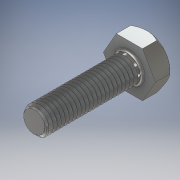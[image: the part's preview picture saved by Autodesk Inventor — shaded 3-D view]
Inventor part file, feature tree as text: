
AUTODESK INVENTOR PART (.ipt)
format: ipt  version: 2017 (Build 210142000, 142)  size: 576,512 bytes
history: native  units: mm
features: sketch x4, extrude x3, chamfer x1, fillet x1, plane x1, helix x1
ambient origin geometry x8: Origin, YZ Plane, XZ Plane, XY Plane, X Axis, Y Axis, Z Axis, Center Point
bodies: Solid1 (feature_tree)
feature tree (11):
  extrude  "Extrusion1"  Depth=7.5mm TaperAngle=0.0deg
  extrude  "Extrusion2"  Depth=7.5mm TaperAngle=45.0deg
  extrude  "Extrusion3"  Depth=40.0mm TaperAngle=0.0deg
  chamfer  "Chamfer1"  Distance=1.0mm Angle=45.0deg
  fillet  "Fillet1"  Radius=1.0mm
  plane  "Work Plane1"
  helix  "Coil1"  [1 undecoded]
  sketch  "Sketch1"  dims[d0=19.0mm d1=7.5mm d2=0.0mm]
  sketch  "Sketch2"  dims[d3=19.0mm d4=7.5mm d5=45.0deg]
  sketch  "Sketch3"  dims[d6=11.0mm d7=40.0mm d8=0.0mm d9=1.0mm d10=2.0mm d11=45.0deg d12=1.0mm d13=0.0mm]
  sketch  "Sketch4"  dims[d14=1.7mm d15=60.0deg d16=2.0mm d17=0.2mm d18=1.7mm d19=40.0mm d20=10.0mm d21=0.0mm d22=90.0deg d23=90.0deg d24=0.0mm d25=0.0mm]
note: 1 required parameter value undecoded (feature->parameter linkage not recoverable at this tier; creation-order binding heuristic only, values carry confidence <= 0.55)
